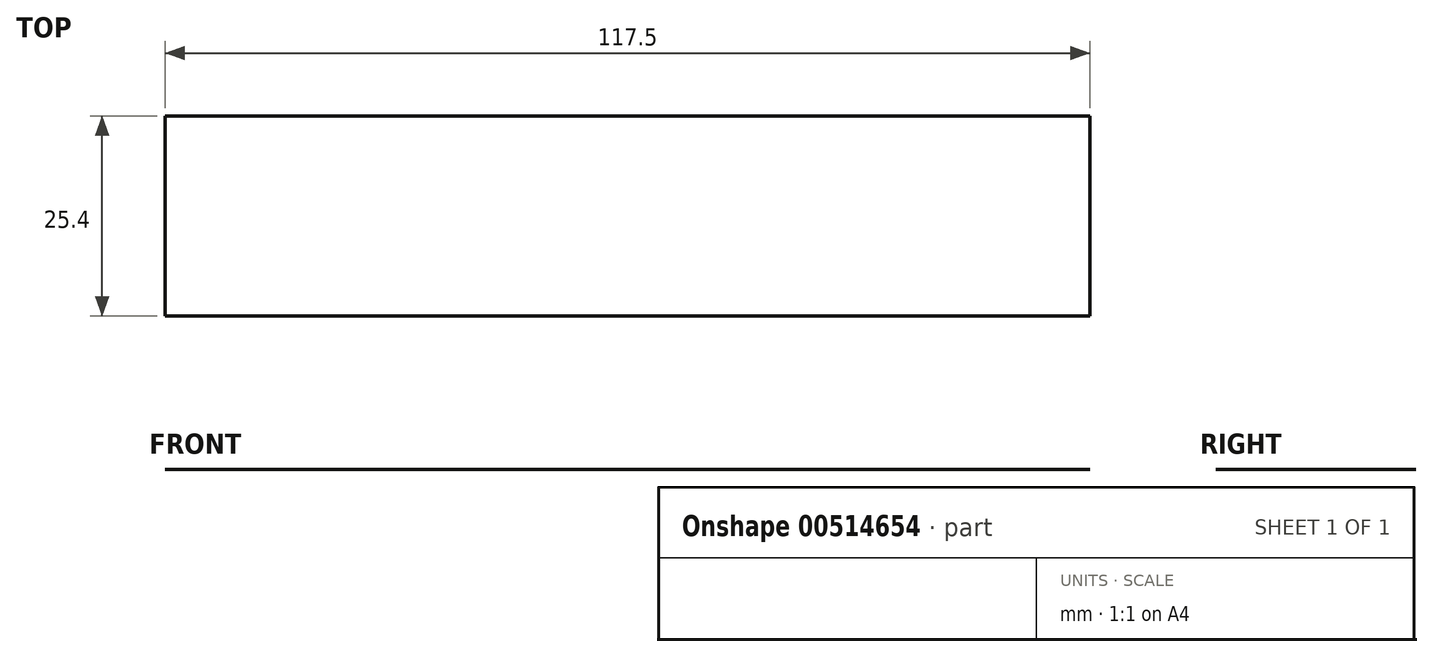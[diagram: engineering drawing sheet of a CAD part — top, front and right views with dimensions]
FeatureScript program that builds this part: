
annotation { "Feature Type Name" : "Feature", "Feature Type Description" : "" }
export const myFeature = defineFeature(function(context is Context, id is Id, definition is map)
    precondition{}
    {
        {
            var Q0;
            Q0=qCreatedBy(makeId("Front.planeOp"),FACE);
            var sketch = newSketch(context, id + "F0", { "sketchPlane" : qUnion([Q0])});
            skLineSegment(sketch, "E0.bottom", {"start": v(-58.1, 45.15) * mm, "end": v(59.41, 45.15) * mm});
            skLineSegment(sketch, "E0.top", {"start": v(-58.1, -30.1) * mm, "end": v(59.41, -30.1) * mm});
            skLineSegment(sketch, "E0.left", {"start": v(-58.1, 45.15) * mm, "end": v(-58.1, -30.1) * mm});
            skLineSegment(sketch, "E0.right", {"start": v(59.41, 45.15) * mm, "end": v(59.41, -30.1) * mm});
            skSolve(sketch);
        }
        {
            var Q0;
            Q0=sQuery(id+"F0.wireOp",EDGE,"E0.bottom");
            extrude(context, id + "F1", {"bodyType" : ToolBodyType.SURFACE, "surfaceEntities" : qUnion([Q0]), "depth" : 25.4 * mm, "offsetDistance" : 25.4 * mm});
        }
    });
